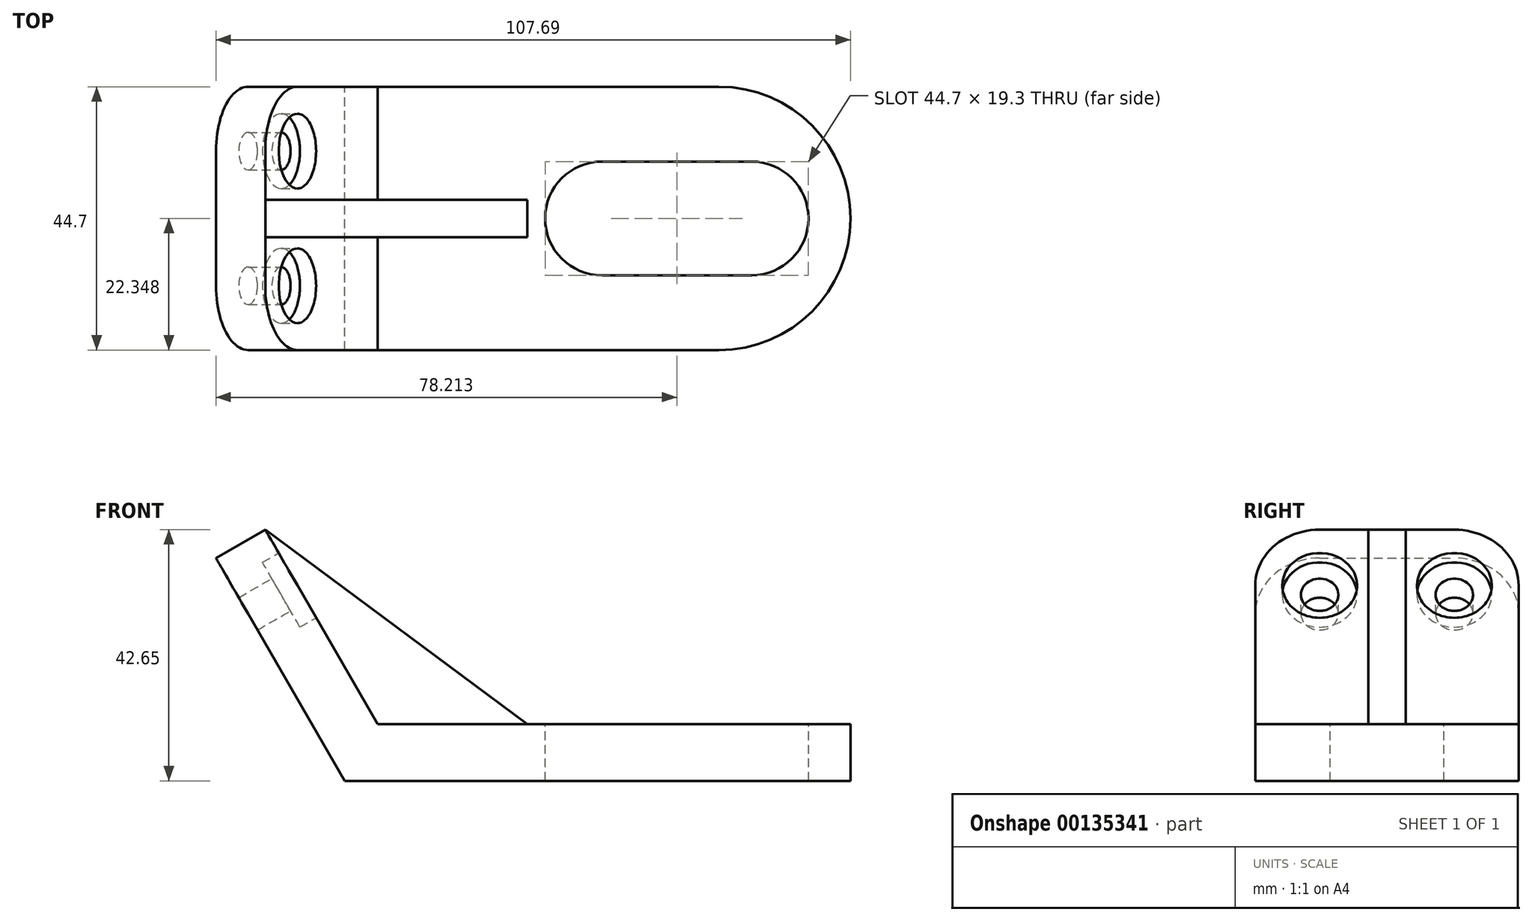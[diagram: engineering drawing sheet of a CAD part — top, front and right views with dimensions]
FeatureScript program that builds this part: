
annotation { "Feature Type Name" : "Feature", "Feature Type Description" : "" }
export const myFeature = defineFeature(function(context is Context, id is Id, definition is map)
    precondition{}
    {
        {
            var Q0;
            Q0=qCreatedBy(makeId("Front.planeOp"),FACE);
            var sketch = newSketch(context, id + "F0", { "sketchPlane" : qUnion([Q0])});
            skLineSegment(sketch, "E0", {"start": v(0, 0) * mm, "end": v(85.85, 0) * mm});
            skLineSegment(sketch, "E1", {"start": v(85.85, 0) * mm, "end": v(85.85, 9.65) * mm});
            skLineSegment(sketch, "E2", {"start": v(-21.84, 37.82) * mm, "end": v(0, 0) * mm});
            skLineSegment(sketch, "E3", {"start": v(-21.84, 37.82) * mm, "end": v(-13.48, 42.65) * mm});
            skLineSegment(sketch, "E4", {"start": v(-13.48, 42.65) * mm, "end": v(5.57, 9.65) * mm});
            skLineSegment(sketch, "E5", {"start": v(5.57, 9.65) * mm, "end": v(85.85, 9.65) * mm});
            skLineSegment(sketch, "E6", {"start": v(-13.48, 42.65) * mm, "end": v(30.97, 9.65) * mm});
            skSolve(sketch);
        }
        {
            var Q0;
            Q0=makeQuery(id+"F0.imprint","IMPRINT",FACE,{"disambiguationData":[TD([[makeQuery(id+"F0.imprint","IMPRINT",EDGE,{"derivedFrom":sQuery(id+"F0.wireOp",EDGE,"E0")}),1.0]])]});
            extrude(context, id + "F1", {"entities" : qUnion([Q0]), "depth" : 44.7 * mm});
        }
        {
            var Q0;
            Q0=makeQuery(id+"F1.opExtrude","SWEPT_FACE",FACE,{"disambiguationData":[OSD([sQuery(id+"F0.wireOp",EDGE,"E5")])]});
            var sketch = newSketch(context, id + "F2", { "sketchPlane" : qUnion([Q0])});
            skLineSegment(sketch, "E7", {"start": v(18.21, -22.35) * mm, "end": v(18.21, -44.7) * mm});
            skLineSegment(sketch, "E8", {"start": v(97.9, -22.35) * mm, "end": v(-62.53, -22.35) * mm, "construction": true});
            skLineSegment(sketch, "E9", {"start": v(43.67, 24.79) * mm, "end": v(43.67, -64.32) * mm, "construction": true});
            skLineSegment(sketch, "E10", {"start": v(69.07, 25.62) * mm, "end": v(69.07, -65.37) * mm, "construction": true});
            skArc(sketch, "E11", {"start": v(69.07, -32) * mm, "mid": v(78.72, -22.35) * mm, "end": v(69.07, -12.7) * mm});
            skLineSegment(sketch, "E12", {"start": v(56.37, 32.21) * mm, "end": v(56.37, -71.95) * mm, "construction": true});
            skArc(sketch, "E13.MirrorCS", {"start": v(43.67, -32) * mm, "mid": v(34.02, -22.35) * mm, "end": v(43.67, -12.7) * mm});
            skLineSegment(sketch, "E14", {"start": v(43.67, -12.7) * mm, "end": v(69.07, -12.7) * mm});
            skLineSegment(sketch, "E15", {"start": v(43.67, -32) * mm, "end": v(69.07, -32) * mm});
            skLineSegment(sketch, "E16.0", {"start": v(5.57, 0) * mm, "end": v(85.85, 0) * mm});
            skLineSegment(sketch, "E17.0", {"start": v(85.85, -44.7) * mm, "end": v(85.85, 0) * mm});
            skLineSegment(sketch, "E18.0", {"start": v(5.57, -44.7) * mm, "end": v(85.85, -44.7) * mm});
            skSolve(sketch);
        }
        {
            var Q0;
            Q0=makeQuery(id+"F1.opExtrude","CAP_EDGE",EDGE,{"disambiguationData":[OSD([sQuery(id+"F0.wireOp",EDGE,"E1")])],"isStart":false});
            var Q1;
            Q1=makeQuery(id+"F1.opExtrude","CAP_EDGE",EDGE,{"disambiguationData":[OSD([sQuery(id+"F0.wireOp",EDGE,"E1")])],"isStart":true});
            fillet(context, id + "F3", {"entities" : qUnion([Q0, Q1]), "radius" : 22.35 * mm, "tangentPropagation" : true, "allowEdgeOverflow" : false});
        }
        {
            var Q0;
            Q0=makeQuery(id+"F1.opExtrude","SWEPT_FACE",FACE,{"disambiguationData":[OSD([sQuery(id+"F0.wireOp",EDGE,"E4")])]});
            var sketch = newSketch(context, id + "F4", { "sketchPlane" : qUnion([Q0])});
            skLineSegment(sketch, "E19", {"start": v(-69.84, 32.75) * mm, "end": v(26.98, 32.75) * mm, "construction": true});
            skLineSegment(sketch, "E20", {"start": v(-10.92, 48.65) * mm, "end": v(-10.92, 17.24) * mm, "construction": true});
            skLineSegment(sketch, "E21", {"start": v(-33.78, 48.65) * mm, "end": v(-33.78, 17.8) * mm, "construction": true});
            skPoint(sketch, "E22", {"position": v(-33.78, 32.75) * mm});
            skPoint(sketch, "E23", {"position": v(-10.92, 32.75) * mm});
            skCircle(sketch, "E24", {"center": v(-33.78, 32.75) * mm, "radius": 3.18 * mm});
            skCircle(sketch, "E25", {"center": v(-10.92, 32.75) * mm, "radius": 3.18 * mm});
            skCircle(sketch, "E26", {"center": v(-33.78, 32.75) * mm, "radius": 6.35 * mm});
            skCircle(sketch, "E27", {"center": v(-10.92, 32.75) * mm, "radius": 6.35 * mm});
            skSolve(sketch);
        }
        {
            var Q0;
            Q0=makeQuery(id+"F1.opExtrude","CAP_EDGE",EDGE,{"disambiguationData":[OSD([sQuery(id+"F0.wireOp",EDGE,"E3")])],"isStart":false});
            var Q1;
            Q1=makeQuery(id+"F1.opExtrude","CAP_EDGE",EDGE,{"disambiguationData":[OSD([sQuery(id+"F0.wireOp",EDGE,"E3")])],"isStart":true});
            fillet(context, id + "F5", {"entities" : qUnion([Q0, Q1]), "radius" : 10.92 * mm, "tangentPropagation" : true, "allowEdgeOverflow" : false});
        }
        {
            var Q0;
            Q0=makeQuery(id+"F4.imprint","IMPRINT",FACE,{"disambiguationData":[TD([[makeQuery(id+"F4.imprint","IMPRINT",EDGE,{"derivedFrom":sQuery(id+"F4.wireOp",EDGE,"E24")}),1.0]])]});
            var Q1;
            Q1=makeQuery(id+"F4.imprint","IMPRINT",FACE,{"disambiguationData":[TD([[makeQuery(id+"F4.imprint","IMPRINT",EDGE,{"derivedFrom":sQuery(id+"F4.wireOp",EDGE,"E25")}),1.0]])]});
            extrude(context, id + "F6", {"entities" : qUnion([Q0, Q1]), "operationType" : NewBodyOperationType.REMOVE, "endBound" : BoundingType.THROUGH_ALL, "oppositeDirection" : true, "depth" : 25.4 * mm});
        }
        {
            var Q0;
            Q0=makeQuery(id+"F4.imprint","IMPRINT",FACE,{"disambiguationData":[TD([[makeQuery(id+"F4.imprint","IMPRINT",EDGE,{"derivedFrom":sQuery(id+"F4.wireOp",EDGE,"E24")}),-1.0]])]});
            var Q1;
            Q1=makeQuery(id+"F4.imprint","IMPRINT",FACE,{"disambiguationData":[TD([[makeQuery(id+"F4.imprint","IMPRINT",EDGE,{"derivedFrom":sQuery(id+"F4.wireOp",EDGE,"E25")}),-1.0]])]});
            extrude(context, id + "F7", {"entities" : qUnion([Q0, Q1]), "operationType" : NewBodyOperationType.REMOVE, "oppositeDirection" : true, "depth" : 3.17 * mm});
        }
        {
            var Q0;
            Q0=makeQuery(id+"F2.imprint","IMPRINT",FACE,{"disambiguationData":[TD([[makeQuery(id+"F2.imprint","IMPRINT",EDGE,{"derivedFrom":sQuery(id+"F2.wireOp",EDGE,"E11")}),1.0]])]});
            extrude(context, id + "F8", {"entities" : qUnion([Q0]), "operationType" : NewBodyOperationType.REMOVE, "endBound" : BoundingType.THROUGH_ALL, "oppositeDirection" : true, "depth" : 25.4 * mm});
        }
        {
            var Q0;
            Q0=qCreatedBy(makeId("Front.planeOp"),FACE);
            cPlane(context, id + "F9", {"entities" : qUnion([Q0]), "cplaneType" : CPlaneType.OFFSET, "offset" : 22.35 * mm, "width" : 152.4 * mm, "height" : 152.4 * mm});
        }
        {
            var Q0;
            Q0=qCreatedBy(id+"F9.planeOp",FACE);
            var sketch = newSketch(context, id + "F10", { "sketchPlane" : qUnion([Q0])});
            skLineSegment(sketch, "E28", {"start": v(-13.48, 42.65) * mm, "end": v(30.97, 9.65) * mm});
            skLineSegment(sketch, "E29", {"start": v(-13.48, 42.65) * mm, "end": v(5.57, 9.65) * mm});
            skLineSegment(sketch, "E30", {"start": v(5.57, 9.65) * mm, "end": v(30.97, 9.65) * mm});
            skLineSegment(sketch, "E31.0", {"start": v(-8.02, 33.19) * mm, "end": v(5.57, 9.65) * mm});
            skLineSegment(sketch, "E32.0", {"start": v(5.57, 9.65) * mm, "end": v(63.5, 9.65) * mm});
            skLineSegment(sketch, "E33.0", {"start": v(-13.48, 42.65) * mm, "end": v(-8.02, 33.19) * mm});
            skSolve(sketch);
        }
        {
            var Q0;
            Q0 = qSketchRegion(id + "F10", true);
            extrude(context, id + "F11", {"entities" : qUnion([Q0]), "operationType" : NewBodyOperationType.ADD, "endBound" : BoundingType.SYMMETRIC, "depth" : 6.35 * mm});
        }
    });
